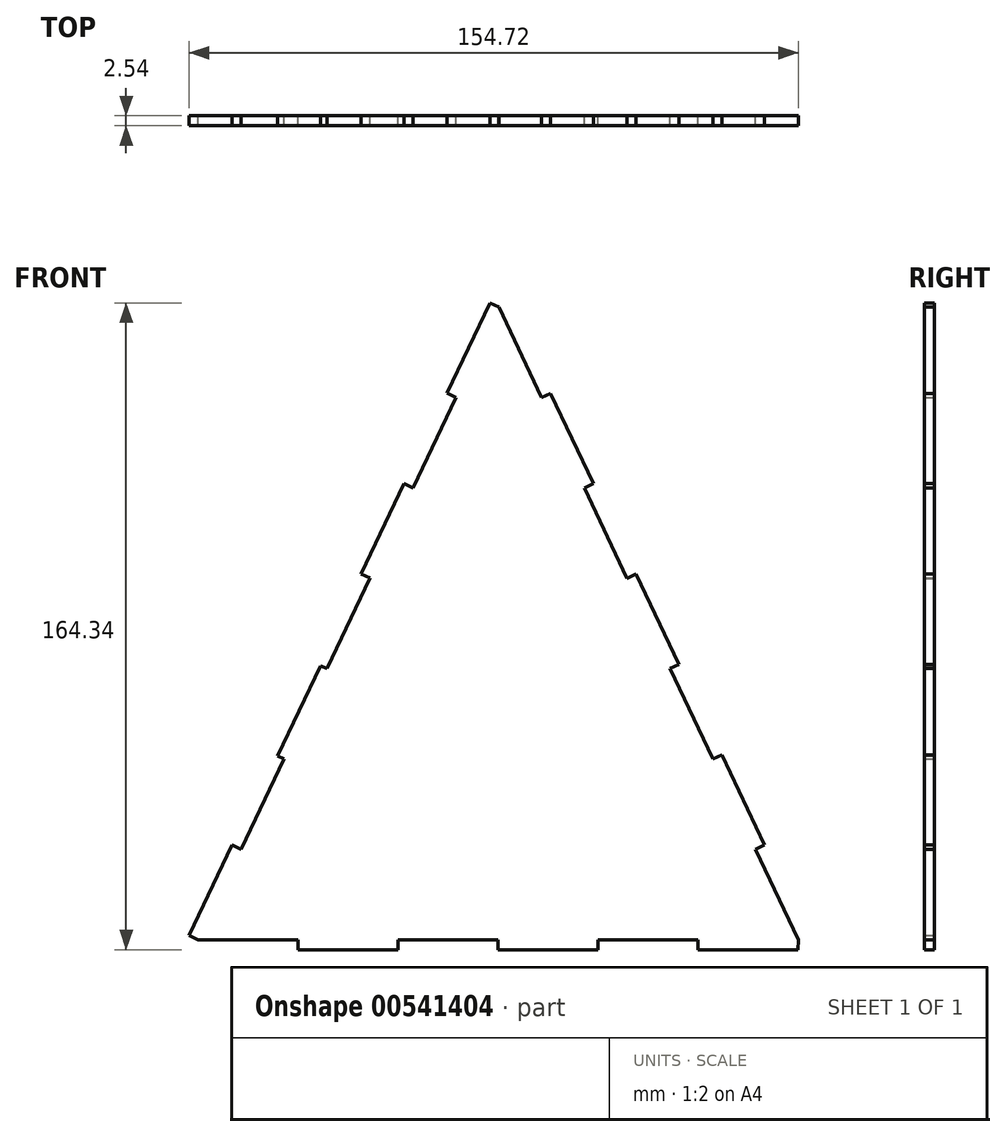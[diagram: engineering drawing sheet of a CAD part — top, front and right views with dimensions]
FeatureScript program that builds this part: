
annotation { "Feature Type Name" : "Feature", "Feature Type Description" : "" }
export const myFeature = defineFeature(function(context is Context, id is Id, definition is map)
    precondition{}
    {
        {
            var Q0;
            Q0=qCreatedBy(makeId("Front.planeOp"),FACE);
            var sketch = newSketch(context, id + "F0", { "sketchPlane" : qUnion([Q0])});
            skLineSegment(sketch, "E0", {"start": v(-10.9, 63.99) * mm, "end": v(-54.56, -27.9) * mm});
            skLineSegment(sketch, "E1", {"start": v(-76.36, -73.78) * mm, "end": v(76.06, -73.78) * mm});
            skLineSegment(sketch, "E2", {"start": v(76.06, -73.78) * mm, "end": v(0, 86.93) * mm});
            skLineSegment(sketch, "E3", {"start": v(0, 86.93) * mm, "end": v(-2.3, 88.02) * mm});
            skLineSegment(sketch, "E4", {"start": v(-2.3, 88.02) * mm, "end": v(-13.2, 65.08) * mm});
            skLineSegment(sketch, "E5", {"start": v(-13.2, 65.08) * mm, "end": v(-10.9, 63.99) * mm});
            skLineSegment(sketch, "E6", {"start": v(-24.1, 42.14) * mm, "end": v(-35, 19.2) * mm});
            skLineSegment(sketch, "E7", {"start": v(-35, 19.2) * mm, "end": v(-32.7, 18.1) * mm});
            skLineSegment(sketch, "E8", {"start": v(-43.6, -4.84) * mm, "end": v(-45.27, -4.19) * mm});
            skLineSegment(sketch, "E9", {"start": v(-45.27, -4.19) * mm, "end": v(-56.17, -27.13) * mm});
            skLineSegment(sketch, "E10", {"start": v(-56.17, -27.13) * mm, "end": v(-54.56, -27.9) * mm});
            skLineSegment(sketch, "E11", {"start": v(-54.56, -27.9) * mm, "end": v(-65.46, -50.84) * mm});
            skLineSegment(sketch, "E12", {"start": v(-65.46, -50.84) * mm, "end": v(-67.76, -49.75) * mm});
            skLineSegment(sketch, "E13", {"start": v(-67.76, -49.75) * mm, "end": v(-78.66, -72.7) * mm});
            skLineSegment(sketch, "E14", {"start": v(-78.66, -72.7) * mm, "end": v(-76.36, -73.78) * mm});
            skLineSegment(sketch, "E15", {"start": v(-76.36, -73.78) * mm, "end": v(-50.96, -73.78) * mm});
            skLineSegment(sketch, "E16", {"start": v(-50.96, -73.78) * mm, "end": v(-50.96, -76.32) * mm});
            skLineSegment(sketch, "E17", {"start": v(-50.96, -76.32) * mm, "end": v(-25.56, -76.32) * mm});
            skLineSegment(sketch, "E18", {"start": v(-25.56, -76.32) * mm, "end": v(-25.56, -73.78) * mm});
            skLineSegment(sketch, "E19", {"start": v(-25.56, -73.78) * mm, "end": v(-0.15, -73.78) * mm});
            skLineSegment(sketch, "E20", {"start": v(-0.15, -73.78) * mm, "end": v(-0.15, -76.32) * mm});
            skLineSegment(sketch, "E21", {"start": v(-0.15, -76.32) * mm, "end": v(25.25, -76.32) * mm});
            skLineSegment(sketch, "E22", {"start": v(25.25, -76.32) * mm, "end": v(25.25, -73.78) * mm});
            skLineSegment(sketch, "E23", {"start": v(25.25, -73.78) * mm, "end": v(50.65, -73.78) * mm});
            skLineSegment(sketch, "E24", {"start": v(50.65, -73.78) * mm, "end": v(50.65, -76.32) * mm});
            skPoint(sketch, "E25", {"position": v(78.35, 9.9) * mm});
            skLineSegment(sketch, "E26", {"start": v(50.65, -76.32) * mm, "end": v(76.05, -76.32) * mm});
            skLineSegment(sketch, "E27", {"start": v(76.05, -76.32) * mm, "end": v(76.06, -73.78) * mm});
            skLineSegment(sketch, "E28", {"start": v(76.06, -73.78) * mm, "end": v(65.2, -50.82) * mm});
            skLineSegment(sketch, "E29", {"start": v(65.2, -50.82) * mm, "end": v(67.5, -49.74) * mm});
            skLineSegment(sketch, "E30", {"start": v(67.5, -49.74) * mm, "end": v(56.62, -26.78) * mm});
            skLineSegment(sketch, "E31", {"start": v(56.62, -26.78) * mm, "end": v(54.33, -27.86) * mm});
            skLineSegment(sketch, "E32", {"start": v(43.46, -4.9) * mm, "end": v(45.76, -3.82) * mm});
            skLineSegment(sketch, "E33", {"start": v(45.76, -3.82) * mm, "end": v(34.9, 19.14) * mm});
            skLineSegment(sketch, "E34", {"start": v(34.9, 19.14) * mm, "end": v(32.6, 18.05) * mm});
            skLineSegment(sketch, "E35", {"start": v(21.73, 41.01) * mm, "end": v(24.03, 42.1) * mm});
            skLineSegment(sketch, "E36", {"start": v(24.03, 42.1) * mm, "end": v(13.16, 65.06) * mm});
            skLineSegment(sketch, "E37", {"start": v(13.16, 65.06) * mm, "end": v(10.87, 63.97) * mm});
            skLineSegment(sketch, "E38.trimOffspring", {"start": v(-65.46, -50.84) * mm, "end": v(-76.36, -73.78) * mm});
            skLineSegment(sketch, "E39", {"start": v(0, 86.93) * mm, "end": v(-10.9, 63.99) * mm});
            skLineSegment(sketch, "E40", {"start": v(-24.1, 42.14) * mm, "end": v(-21.8, 41.05) * mm});
            skSolve(sketch);
        }
        {
            var Q0;
            Q0=qSketchRegion(id+"F0",true);
            extrude(context, id + "F1", {"entities" : qUnion([Q0]), "depth" : 2.54 * mm, "offsetDistance" : 25.4 * mm});
        }
    });
